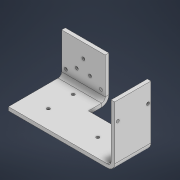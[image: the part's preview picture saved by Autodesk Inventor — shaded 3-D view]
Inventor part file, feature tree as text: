
AUTODESK INVENTOR PART (.ipt)
format: ipt  version: 2021 (Build 250183000, 183)  size: 217,088 bytes
history: native  units: mm
features: sheet_metal_op x9, sketch x7, other x4, hole x3, mirror x1, plane x1, split x1
ambient origin geometry x8: Origin, YZ Plane, XZ Plane, XY Plane, X Axis, Y Axis, Z Axis, Center Point
bodies: Solid1 (feature_tree)
feature tree (26):
  sheet_metal_op  "Face1"
  sheet_metal_op  "Flange1"
  sheet_metal_op  "Face2"
  sheet_metal_op  "Flange2"
  hole  "Hole1"  [1 undecoded]
  hole  "Hole2"  [1 undecoded]
  hole  "Hole3"  [1 undecoded]
  mirror  "Mirror1"
  plane  "Work Plane1"
  split  "Split1"
  sketch  "Sketch1"  dims[d0=72.0mm d1=36.0mm]
  other  "Plate1"
  sketch  "Sketch2"  dims[d2=72.0mm d3=36.0mm]
  other  "Plate2"
  sheet_metal_op  "Bend1"
  sheet_metal_op  "Corner1"
  sketch  "Sketch3"  dims[d4=6.0mm d5=6.0mm]
  other  "Plate3"
  sheet_metal_op  "Bend2"
  sketch  "Sketch4"  dims[d6=3.0mm]
  other  "Plate4"
  sheet_metal_op  "Bend3"
  sheet_metal_op  "Corner2"
  sketch  "Sketch5"  dims[d7=12.0mm]
  sketch  "Sketch6"  dims[d8=6.0mm]
  sketch  "Sketch7"  dims[d9=94.0mm d10=90.0deg d11=6.0mm d12=24.0mm d13=6.0mm d14=6.0mm d15=103.7mm d16=60.0mm d17=6.0mm d18=6.0mm d19=3.0mm d20=12.0mm d21=6.0mm d22=6.0mm d23=3.0mm d24=12.0mm d25=6.0mm d26=100.6mm d27=90.0deg d28=6.0mm d29=24.0mm d30=6.0mm d31=6.0mm d32=60.0mm d33=30.0mm d34=30.0mm d35=50.0mm d36=30.0mm d37=30.0mm d38=5.0mm d39=6.0mm d40=4.0mm d41=2.0mm d42=90.0deg d43=6.0mm d44=0.0mm d45=36.0mm d46=25.4mm d47=67.0mm d48=120.0deg d49=120.0deg d50=0.0mm d51=5.0mm d52=6.0mm d53=4.0mm d54=2.0mm d55=90.0deg d56=6.0mm d57=0.0mm d58=5.0mm d59=6.0mm d60=4.0mm d61=2.0mm d62=90.0deg d63=6.0mm d64=0.0mm d65=60.0mm d66=72.0mm d67=30.0mm d68=30.0mm d69=36.0mm d70=22.0mm d71=11.0mm d72=36.0mm d73=91.7mm d74=45.85mm]
note: 3 required parameter values undecoded (feature->parameter linkage not recoverable at this tier; creation-order binding heuristic only, values carry confidence <= 0.55)
